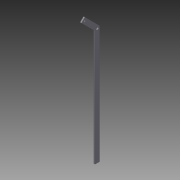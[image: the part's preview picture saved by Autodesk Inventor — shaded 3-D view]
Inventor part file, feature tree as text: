
AUTODESK INVENTOR PART (.ipt)
format: ipt  version: 2014 (Build 180170000, 170)  size: 80,896 bytes
history: native  units: in
note: dims shown in document units (in); Inventor stores cm internally (conversion verified against a paired STEP export)
features: extrude x1, sketch x1
ambient origin geometry x8: Origin, YZ Plane, XZ Plane, XY Plane, X Axis, Y Axis, Z Axis, Center Point
bodies: Solid1 (feature_tree)
feature tree (2):
  extrude  "Extrusion1"  Depth=0.25in
  sketch  "Sketch1"  dims[d0=1.0in d7=24.0in d8=4.0in d9=135.0deg d10=1.0in d11=0.5in d12=0.25in d13=0.5in d14=0.5in d15=0.25in d16=0.0in]
